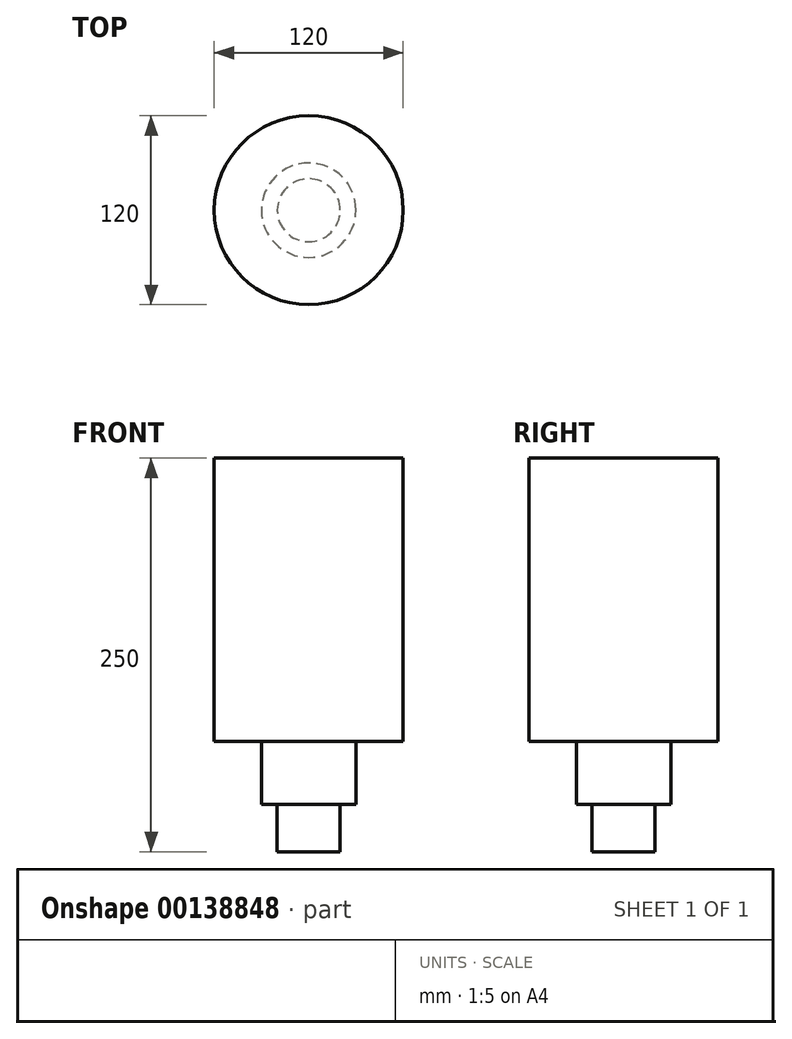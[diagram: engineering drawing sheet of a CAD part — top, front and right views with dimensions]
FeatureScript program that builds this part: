
annotation { "Feature Type Name" : "Feature", "Feature Type Description" : "" }
export const myFeature = defineFeature(function(context is Context, id is Id, definition is map)
    precondition{}
    {
        {
            var Q0;
            Q0=qCreatedBy(makeId("Top.planeOp"),FACE);
            var sketch = newSketch(context, id + "F0", { "sketchPlane" : qUnion([Q0])});
            skCircle(sketch, "E0", {"center": v(0, 0) * mm, "radius": 20 * mm});
            skSolve(sketch);
        }
        {
            var Q0;
            Q0 = qSketchRegion(id + "F0", true);
            extrude(context, id + "F1", {"entities" : qUnion([Q0]), "oppositeDirection" : true, "depth" : 30 * mm});
        }
        {
            var Q0;
            Q0=qCreatedBy(makeId("Top.planeOp"),FACE);
            var sketch = newSketch(context, id + "F2", { "sketchPlane" : qUnion([Q0])});
            skCircle(sketch, "E1", {"center": v(0, 0) * mm, "radius": 30 * mm});
            skSolve(sketch);
        }
        {
            var Q0;
            Q0 = qSketchRegion(id + "F2", true);
            extrude(context, id + "F3", {"entities" : qUnion([Q0]), "operationType" : NewBodyOperationType.ADD, "depth" : 40 * mm});
        }
        {
            var Q0;
            Q0=makeQuery(id+"F3.opExtrude","CAP_FACE",FACE,{"disambiguationData":[OSD([sQuery(id+"F2.wireOp",EDGE,"E1")])],"isStart":false});
            var sketch = newSketch(context, id + "F4", { "sketchPlane" : qUnion([Q0])});
            skCircle(sketch, "E2", {"center": v(0, 0) * mm, "radius": 60 * mm});
            skSolve(sketch);
        }
        {
            var Q0;
            Q0 = qSketchRegion(id + "F4", true);
            extrude(context, id + "F5", {"entities" : qUnion([Q0]), "operationType" : NewBodyOperationType.ADD, "depth" : 180 * mm});
        }
    });
